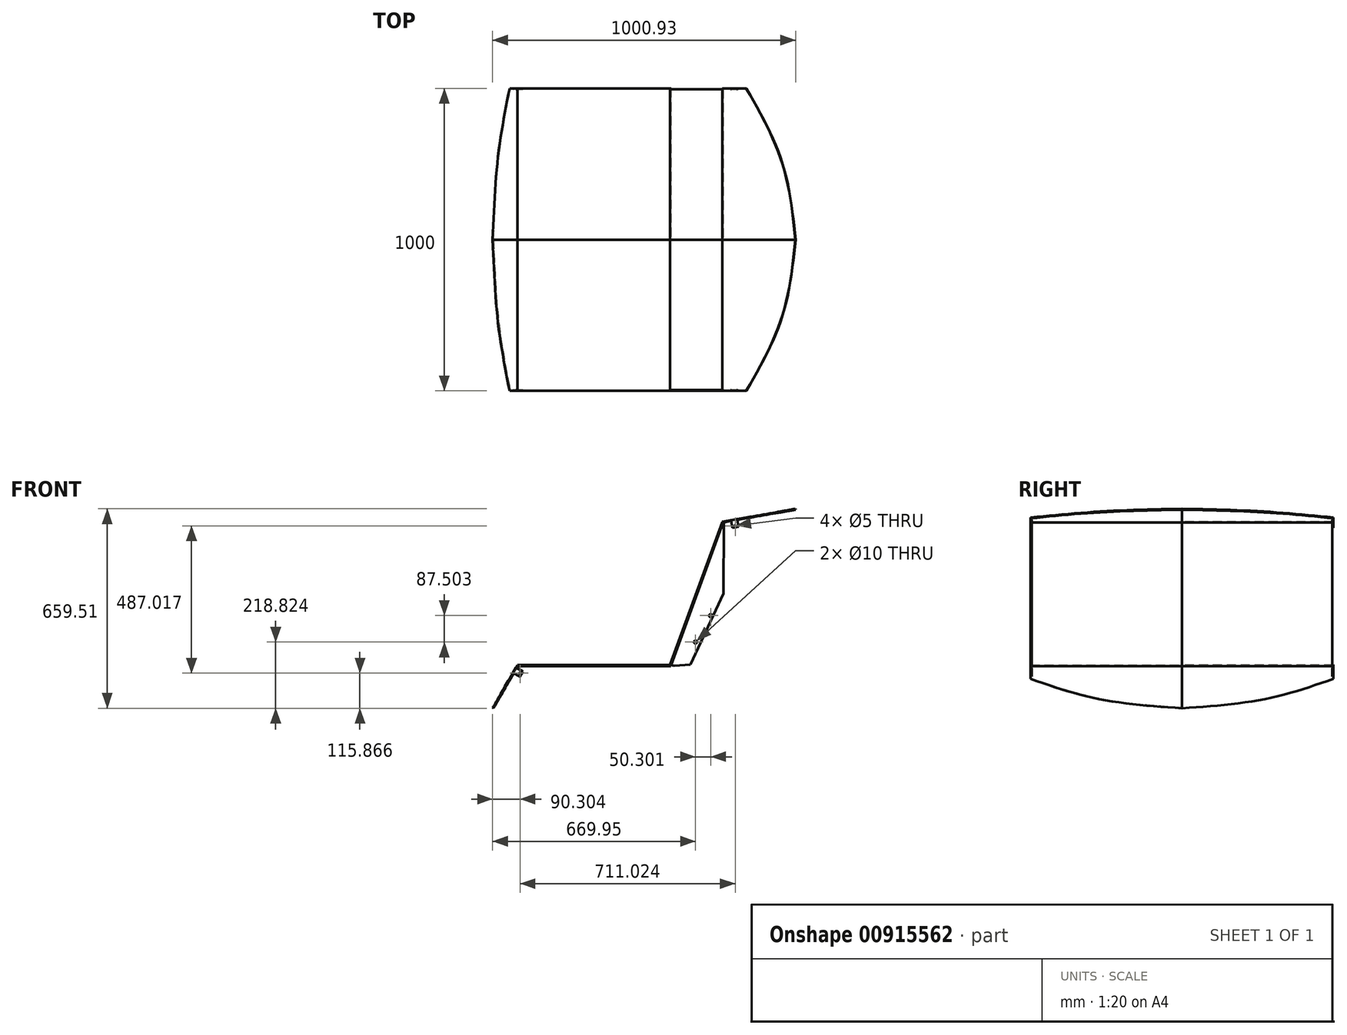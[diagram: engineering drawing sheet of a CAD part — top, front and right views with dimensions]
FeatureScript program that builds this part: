
annotation { "Feature Type Name" : "Feature", "Feature Type Description" : "" }
export const myFeature = defineFeature(function(context is Context, id is Id, definition is map)
    precondition{}
    {
        {
            var Q0;
            Q0=qCreatedBy(makeId("Front.planeOp"),FACE);
            var sketch = newSketch(context, id + "F0", { "sketchPlane" : qUnion([Q0])});
            skLineSegment(sketch, "E0", {"start": v(0, 0) * mm, "end": v(504.47, 0) * mm});
            skLineSegment(sketch, "E1", {"start": v(0, 0) * mm, "end": v(-81.6, -141.33) * mm});
            skLineSegment(sketch, "E2", {"start": v(504.47, 0) * mm, "end": v(677, 474.05) * mm});
            skLineSegment(sketch, "E3", {"start": v(677, 474.05) * mm, "end": v(918.8, 516.68) * mm});
            skLineSegment(sketch, "E4.0", {"start": v(679.24, 471.4) * mm, "end": v(919.33, 513.73) * mm});
            skLineSegment(sketch, "E4.1", {"start": v(506.57, -3) * mm, "end": v(679.24, 471.4) * mm});
            skLineSegment(sketch, "E4.2", {"start": v(1.73, -3) * mm, "end": v(506.57, -3) * mm});
            skLineSegment(sketch, "E4.3", {"start": v(1.73, -3) * mm, "end": v(-79, -142.83) * mm});
            skLineSegment(sketch, "E5", {"start": v(-79, -142.83) * mm, "end": v(-81.6, -141.33) * mm});
            skLineSegment(sketch, "E6", {"start": v(919.33, 513.73) * mm, "end": v(918.8, 516.68) * mm});
            skSolve(sketch);
        }
        {
            var Q0;
            Q0=makeQuery(id+"F0.imprint","IMPRINT",FACE,{"disambiguationData":[TD([[makeQuery(id+"F0.imprint","IMPRINT",EDGE,{"derivedFrom":sQuery(id+"F0.wireOp",EDGE,"E0")}),-1.0]])]});
            extrude(context, id + "F1", {"entities" : qUnion([Q0]), "depth" : 500 * mm, "offsetDistance" : 25 * mm});
        }
        {
            var Q0;
            Q0=makeQuery(id+"F1.opExtrude","SWEPT_FACE",FACE,{"disambiguationData":[OSD([sQuery(id+"F0.wireOp",EDGE,"E1")])]});
            var sketch = newSketch(context, id + "F2", { "sketchPlane" : qUnion([Q0])});
            skLineSegment(sketch, "E7", {"start": v(0, -163.2) * mm, "end": v(0, 586.8) * mm, "construction": true});
            skLineSegment(sketch, "E8", {"start": v(500, 0) * mm, "end": v(500, -51.4) * mm, "construction": true});
            skFitSpline(sketch, "E9", {"points": [v(0, -163.2) * mm, v(271.48, -128.56) * mm, v(500, -51.4) * mm], "startDerivative": vector(540.37, 43.35) * mm, "endDerivative": vector(458.78, 181.7) * mm});
            skLineSegment(sketch, "E10", {"start": v(500, -51.4) * mm, "end": v(528.77, -51.4) * mm});
            skLineSegment(sketch, "E11", {"start": v(528.77, -51.4) * mm, "end": v(528.77, -174.68) * mm});
            skLineSegment(sketch, "E12", {"start": v(528.77, -174.68) * mm, "end": v(0, -174.68) * mm});
            skLineSegment(sketch, "E13", {"start": v(0, -174.68) * mm, "end": v(0, -163.2) * mm});
            skSolve(sketch);
        }
        {
            var Q0;
            Q0 = qSketchRegion(id + "F2", true);
            extrude(context, id + "F3", {"entities" : qUnion([Q0]), "operationType" : NewBodyOperationType.REMOVE, "oppositeDirection" : true, "depth" : 25 * mm, "offsetDistance" : 25 * mm});
        }
        {
            var Q0;
            Q0=makeQuery(id+"F1.opExtrude","SWEPT_FACE",FACE,{"disambiguationData":[OSD([sQuery(id+"F0.wireOp",EDGE,"E3")])]});
            var sketch = newSketch(context, id + "F4", { "sketchPlane" : qUnion([Q0])});
            skLineSegment(sketch, "E14", {"start": v(749.04, -500) * mm, "end": v(829.72, -500) * mm, "construction": true});
            skFitSpline(sketch, "E15", {"points": [v(994.57, 0) * mm, v(948.78, -256.82) * mm, v(829.72, -500) * mm], "startDerivative": vector(-56.9, -527.53) * mm, "endDerivative": vector(-272.14, -472.64) * mm});
            skLineSegment(sketch, "E16", {"start": v(994.57, 0) * mm, "end": v(1016.99, 0) * mm});
            skLineSegment(sketch, "E17", {"start": v(1016.99, 0) * mm, "end": v(1016.99, -521.85) * mm});
            skLineSegment(sketch, "E18", {"start": v(1016.99, -521.85) * mm, "end": v(833.8, -521.85) * mm});
            skLineSegment(sketch, "E19", {"start": v(833.8, -521.85) * mm, "end": v(829.72, -500) * mm});
            skSolve(sketch);
        }
        {
            var Q0;
            {var subQ0=sQuery(id+"F4.wireOp",EDGE,"E15");Q0=makeQuery(id+"F4.imprint","IMPRINT",FACE,{"disambiguationData":[TD([[makeQuery(id+"F4.imprint","IMPRINT",EDGE,{"derivedFrom":subQ0}),1.0]])]});}
            extrude(context, id + "F5", {"entities" : qUnion([Q0]), "operationType" : NewBodyOperationType.REMOVE, "oppositeDirection" : true, "depth" : 25 * mm, "offsetDistance" : 25 * mm});
        }
        {
            var Q0;
            Q0=makeQuery(id+"F1.opExtrude","SWEPT_FACE",FACE,{"disambiguationData":[OSD([sQuery(id+"F0.wireOp",EDGE,"E1")])]});
            var sketch = newSketch(context, id + "F6", { "sketchPlane" : qUnion([Q0])});
            skLineSegment(sketch, "E20", {"start": v(500, -51.4) * mm, "end": v(500, -30) * mm, "construction": true});
            skLineSegment(sketch, "E21", {"start": v(500, -30) * mm, "end": v(497, -30) * mm});
            skLineSegment(sketch, "E22", {"start": v(497, -30) * mm, "end": v(497, -8) * mm});
            skLineSegment(sketch, "E23", {"start": v(497, -8) * mm, "end": v(500, -8) * mm});
            skLineSegment(sketch, "E24", {"start": v(500, -8) * mm, "end": v(500, -30) * mm});
            skSolve(sketch);
        }
        {
            var Q0;
            Q0 = qSketchRegion(id + "F6", true);
            extrude(context, id + "F7", {"entities" : qUnion([Q0]), "operationType" : NewBodyOperationType.REMOVE, "oppositeDirection" : true, "depth" : 25 * mm, "offsetDistance" : 25 * mm});
        }
        {
            var Q0;
            Q0=makeQuery(id+"F1.opExtrude","SWEPT_FACE",FACE,{"disambiguationData":[OSD([sQuery(id+"F0.wireOp",EDGE,"E3")])]});
            var sketch = newSketch(context, id + "F8", { "sketchPlane" : qUnion([Q0])});
            skLineSegment(sketch, "E25", {"start": v(749.04, -500) * mm, "end": v(777.68, -500) * mm, "construction": true});
            skLineSegment(sketch, "E26", {"start": v(777.68, -500) * mm, "end": v(777.68, -497) * mm});
            skLineSegment(sketch, "E27", {"start": v(777.68, -497) * mm, "end": v(799.68, -497) * mm});
            skLineSegment(sketch, "E28", {"start": v(799.68, -497) * mm, "end": v(799.68, -500) * mm});
            skPoint(sketch, "E28.endSnap0", {"position": v(763.36, -500) * mm});
            skLineSegment(sketch, "E29", {"start": v(799.68, -500) * mm, "end": v(777.68, -500) * mm});
            skSolve(sketch);
        }
        {
            var Q0;
            Q0=makeQuery(id+"F8.imprint","IMPRINT",FACE,{"disambiguationData":[TD([[makeQuery(id+"F8.imprint","IMPRINT",EDGE,{"derivedFrom":sQuery(id+"F8.wireOp",EDGE,"E26")}),-1.0]])]});
            extrude(context, id + "F9", {"entities" : qUnion([Q0]), "operationType" : NewBodyOperationType.REMOVE, "oppositeDirection" : true, "depth" : 25 * mm, "offsetDistance" : 25 * mm});
        }
        {
            var Q0;
            Q0=makeQuery(id+"F9.boolean.opBoolean","COPY",FACE,{"derivedFrom":makeQuery(id+"F9.opExtrude","SWEPT_FACE",FACE,{"disambiguationData":[OSD([sQuery(id+"F8.wireOp",EDGE,"E27")])]})});
            var sketch = newSketch(context, id + "F10", { "sketchPlane" : qUnion([Q0])});
            skLineSegment(sketch, "E30", {"start": v(726.88, 482.84) * mm, "end": v(725.9, 482.67) * mm, "construction": true});
            skLineSegment(sketch, "E31", {"start": v(705.21, 479.02) * mm, "end": v(706.2, 479.2) * mm, "construction": true});
            skLineSegment(sketch, "E32", {"start": v(725.9, 482.67) * mm, "end": v(730.44, 456.86) * mm});
            skLineSegment(sketch, "E33", {"start": v(730.44, 456.86) * mm, "end": v(710.75, 453.4) * mm});
            skLineSegment(sketch, "E34", {"start": v(710.75, 453.4) * mm, "end": v(706.2, 479.2) * mm});
            skLineSegment(sketch, "E35", {"start": v(725.9, 482.67) * mm, "end": v(706.2, 479.2) * mm});
            skSolve(sketch);
        }
        {
            var Q0;
            Q0 = qSketchRegion(id + "F10", true);
            extrude(context, id + "F11", {"entities" : qUnion([Q0]), "operationType" : NewBodyOperationType.ADD, "depth" : 3 * mm, "offsetDistance" : 25 * mm});
        }
        {
            var Q0;
            Q0=makeQuery(id+"F11.opExtrude","CAP_EDGE",EDGE,{"disambiguationData":[OSD([sQuery(id+"F10.wireOp",EDGE,"E35")])],"isStart":false});
            var Q1;
            {var subQ0=makeQuery(id+"F1.opExtrude","SWEPT_FACE",FACE,{"disambiguationData":[OSD([sQuery(id+"F0.wireOp",EDGE,"E4.0")])]});Q1=makeQuery(id+"F11.boolean.opBoolean","SPLIT",EDGE,{"disambiguationData":[topologyDisambiguationEdgeConnected([subQ0,makeQuery(id+"F11.opExtrude","CAP_FACE",FACE,{"disambiguationData":[OSD([sQuery(id+"F10.wireOp",EDGE,"E32"),sQuery(id+"F10.wireOp",EDGE,"E33"),sQuery(id+"F10.wireOp",EDGE,"E34"),sQuery(id+"F10.wireOp",EDGE,"E35")])],"isStart":true})])],"derivedFrom":makeQuery(id+"F9.boolean.opBoolean","INTERSECT",EDGE,{"derivedFrom":[subQ0,makeQuery(id+"F9.opExtrude","SWEPT_FACE",FACE,{"disambiguationData":[OSD([sQuery(id+"F8.wireOp",EDGE,"E27")])]})]})});}
            fillet(context, id + "F12", {"entities" : qUnion([Q0, Q1]), "radius" : 1.5 * mm, "tangentPropagation" : true, "allowEdgeOverflow" : false});
        }
        {
            var Q0;
            Q0=makeQuery(id+"F11.opExtrude","CAP_FACE",FACE,{"disambiguationData":[OSD([sQuery(id+"F10.wireOp",EDGE,"E32"),sQuery(id+"F10.wireOp",EDGE,"E33"),sQuery(id+"F10.wireOp",EDGE,"E34"),sQuery(id+"F10.wireOp",EDGE,"E35")])],"isStart":false});
            var sketch = newSketch(context, id + "F13", { "sketchPlane" : qUnion([Q0])});
            skLineSegment(sketch, "E36", {"start": v(709.88, 458.32) * mm, "end": v(729.58, 461.79) * mm, "construction": true});
            skCircle(sketch, "E37", {"center": v(719.73, 460.05) * mm, "radius": 2.5 * mm});
            skSolve(sketch);
        }
        {
            var Q0;
            Q0=makeQuery(id+"F13.imprint","IMPRINT",FACE,{"disambiguationData":[TD([[makeQuery(id+"F13.imprint","IMPRINT",EDGE,{"derivedFrom":sQuery(id+"F13.wireOp",EDGE,"E37")}),1.0]])]});
            extrude(context, id + "F14", {"entities" : qUnion([Q0]), "operationType" : NewBodyOperationType.REMOVE, "oppositeDirection" : true, "depth" : 25 * mm, "offsetDistance" : 25 * mm});
        }
        {
            var Q0;
            Q0=makeQuery(id+"F7.boolean.opBoolean","COPY",FACE,{"derivedFrom":makeQuery(id+"F7.opExtrude","SWEPT_FACE",FACE,{"disambiguationData":[OSD([sQuery(id+"F6.wireOp",EDGE,"E22")])]})});
            var sketch = newSketch(context, id + "F15", { "sketchPlane" : qUnion([Q0])});
            skLineSegment(sketch, "E38", {"start": v(-4, -6.93) * mm, "end": v(-4.5, -7.8) * mm, "construction": true});
            skLineSegment(sketch, "E39", {"start": v(-15, -25.98) * mm, "end": v(-14.5, -25.11) * mm, "construction": true});
            skLineSegment(sketch, "E40", {"start": v(-14.5, -25.11) * mm, "end": v(-4.5, -7.8) * mm});
            skLineSegment(sketch, "E41", {"start": v(-4.5, -7.8) * mm, "end": v(18.03, -20.8) * mm});
            skPoint(sketch, "E42.end.orphan", {"position": v(0, -29.45) * mm});
            skLineSegment(sketch, "E43", {"start": v(18.03, -20.8) * mm, "end": v(8.03, -38.12) * mm});
            skLineSegment(sketch, "E44", {"start": v(8.03, -38.12) * mm, "end": v(-14.5, -25.11) * mm});
            skSolve(sketch);
        }
        {
            var Q0;
            Q0 = qSketchRegion(id + "F15", true);
            extrude(context, id + "F16", {"entities" : qUnion([Q0]), "operationType" : NewBodyOperationType.ADD, "depth" : 3 * mm, "offsetDistance" : 25 * mm});
        }
        {
            var Q0;
            Q0=makeQuery(id+"F16.opExtrude","CAP_EDGE",EDGE,{"disambiguationData":[OSD([sQuery(id+"F15.wireOp",EDGE,"E40")])],"isStart":false});
            var Q1;
            {var subQ0=makeQuery(id+"F1.opExtrude","SWEPT_FACE",FACE,{"disambiguationData":[OSD([sQuery(id+"F0.wireOp",EDGE,"E4.3")])]});Q1=makeQuery(id+"F16.boolean.opBoolean","SPLIT",EDGE,{"disambiguationData":[topologyDisambiguationEdgeConnected([subQ0,makeQuery(id+"F16.opExtrude","CAP_FACE",FACE,{"disambiguationData":[OSD([sQuery(id+"F15.wireOp",EDGE,"E40"),sQuery(id+"F15.wireOp",EDGE,"E41"),sQuery(id+"F15.wireOp",EDGE,"E43"),sQuery(id+"F15.wireOp",EDGE,"E44")])],"isStart":true})])],"derivedFrom":makeQuery(id+"F7.boolean.opBoolean","INTERSECT",EDGE,{"derivedFrom":[subQ0,makeQuery(id+"F7.opExtrude","SWEPT_FACE",FACE,{"disambiguationData":[OSD([sQuery(id+"F6.wireOp",EDGE,"E22")])]})]})});}
            fillet(context, id + "F17", {"entities" : qUnion([Q0, Q1]), "radius" : 1.5 * mm, "tangentPropagation" : true, "allowEdgeOverflow" : false});
        }
        {
            var Q0;
            Q0=makeQuery(id+"F16.opExtrude","CAP_FACE",FACE,{"disambiguationData":[OSD([sQuery(id+"F15.wireOp",EDGE,"E40"),sQuery(id+"F15.wireOp",EDGE,"E41"),sQuery(id+"F15.wireOp",EDGE,"E43"),sQuery(id+"F15.wireOp",EDGE,"E44")])],"isStart":false});
            var sketch = newSketch(context, id + "F18", { "sketchPlane" : qUnion([Q0])});
            skLineSegment(sketch, "E45", {"start": v(13.7, -18.3) * mm, "end": v(3.7, -35.62) * mm, "construction": true});
            skCircle(sketch, "E46", {"center": v(8.7, -26.96) * mm, "radius": 2.5 * mm});
            skSolve(sketch);
        }
        {
            var Q0;
            Q0 = qSketchRegion(id + "F18", true);
            extrude(context, id + "F19", {"entities" : qUnion([Q0]), "operationType" : NewBodyOperationType.REMOVE, "oppositeDirection" : true, "depth" : 25 * mm, "offsetDistance" : 25 * mm});
        }
        {
            var Q0;
            Q0=makeQuery(id+"F1.opExtrude","SWEPT_FACE",FACE,{"disambiguationData":[OSD([sQuery(id+"F0.wireOp",EDGE,"E2")])]});
            var sketch = newSketch(context, id + "F20", { "sketchPlane" : qUnion([Q0])});
            skLineSegment(sketch, "E47", {"start": v(500, 677) * mm, "end": v(500, 676) * mm, "construction": true});
            skLineSegment(sketch, "E48", {"start": v(500, 676) * mm, "end": v(497, 676) * mm});
            skLineSegment(sketch, "E49", {"start": v(497, 676) * mm, "end": v(497, 173.54) * mm});
            skLineSegment(sketch, "E50", {"start": v(497, 173.54) * mm, "end": v(500, 173.54) * mm});
            skSolve(sketch);
        }
        {
            var Q0;
            Q0 = qSketchRegion(id + "F20", true);
            var Q1;
            {var subQ0=sQuery(id+"F20.wireOp",EDGE,"E48");Q1=makeQuery(id+"F20.imprint","IMPRINT",FACE,{"disambiguationData":[TD([[makeQuery(id+"F20.imprint","IMPRINT",EDGE,{"derivedFrom":subQ0}),1.0]])]});}
            extrude(context, id + "F21", {"entities" : qUnion([Q0, Q1]), "operationType" : NewBodyOperationType.REMOVE, "oppositeDirection" : true, "depth" : 25 * mm, "offsetDistance" : 25 * mm});
        }
        {
            var Q0;
            Q0=makeQuery(id+"F21.boolean.opBoolean","COPY",FACE,{"derivedFrom":makeQuery(id+"F21.opExtrude","SWEPT_FACE",FACE,{"disambiguationData":[OSD([sQuery(id+"F20.wireOp",EDGE,"E49")])]})});
            var sketch = newSketch(context, id + "F22", { "sketchPlane" : qUnion([Q0])});
            skLineSegment(sketch, "E51", {"start": v(676.67, 473.1) * mm, "end": v(676.32, 472.17) * mm, "construction": true});
            skLineSegment(sketch, "E52", {"start": v(676.32, 472.17) * mm, "end": v(681.96, 470.12) * mm});
            skLineSegment(sketch, "E53", {"start": v(601.23, 265.83) * mm, "end": v(680.73, 236.9) * mm, "construction": true});
            skLineSegment(sketch, "E54", {"start": v(676.32, 472.17) * mm, "end": v(755.83, 443.23) * mm, "construction": true});
            skLineSegment(sketch, "E55", {"start": v(679.54, 233.63) * mm, "end": v(755.83, 443.23) * mm, "construction": true});
            skPoint(sketch, "E56.end.orphan", {"position": v(680.68, 337.59) * mm});
            skLineSegment(sketch, "E57", {"start": v(681.96, 470.12) * mm, "end": v(680.73, 236.9) * mm});
            skLineSegment(sketch, "E58", {"start": v(680.73, 236.9) * mm, "end": v(592.08, -6.66) * mm, "construction": true});
            skLineSegment(sketch, "E59", {"start": v(592.08, -6.66) * mm, "end": v(571.2, 0.94) * mm, "construction": true});
            skLineSegment(sketch, "E60", {"start": v(680.73, 236.9) * mm, "end": v(571.2, 0.94) * mm});
            skLineSegment(sketch, "E61", {"start": v(504.81, 0.94) * mm, "end": v(505.15, 1.88) * mm, "construction": true});
            skLineSegment(sketch, "E62", {"start": v(505.15, 1.88) * mm, "end": v(518.28, -2.9) * mm});
            skLineSegment(sketch, "E63", {"start": v(518.28, -2.9) * mm, "end": v(571.2, 0.94) * mm});
            skSolve(sketch);
        }
        {
            var Q0;
            {var subQ0=sQuery(id+"F22.wireOp",EDGE,"E52");var subQ1=sQuery(id+"F20.wireOp",EDGE,"E49");var subQ2=makeQuery(id+"F21.boolean.opBoolean","COPY",EDGE,{"derivedFrom":makeQuery(id+"F21.opExtrude","CAP_EDGE",EDGE,{"disambiguationData":[OSD([subQ1])],"isStart":true})});var subQ3=makeQuery(id+"F22.imprint","INTERSECT",VERTEX,{"derivedFrom":[subQ2,subQ0]});Q0=makeQuery(id+"F22.imprint","IMPRINT",FACE,{"disambiguationData":[TD([[makeQuery(id+"F22.imprint","IMPRINT",EDGE,{"disambiguationData":[TD([[subQ3,-1.0]])],"derivedFrom":subQ2}),1.0]])]});}
            var Q1;
            {var subQ4=sQuery(id+"F22.wireOp",EDGE,"E57");Q1=makeQuery(id+"F22.imprint","IMPRINT",FACE,{"disambiguationData":[TD([[makeQuery(id+"F22.imprint","IMPRINT",EDGE,{"derivedFrom":subQ4}),-1.0]])]});}
            extrude(context, id + "F23", {"entities" : qUnion([Q0, Q1]), "operationType" : NewBodyOperationType.ADD, "depth" : 3 * mm, "offsetDistance" : 25 * mm});
        }
        {
            var Q0;
            Q0=makeQuery(id+"F23.opExtrude","CAP_FACE",FACE,{"disambiguationData":[OSD([sQuery(id+"F20.wireOp",EDGE,"E49"),sQuery(id+"F22.wireOp",EDGE,"E52"),sQuery(id+"F22.wireOp",EDGE,"E57"),sQuery(id+"F22.wireOp",EDGE,"E60"),sQuery(id+"F22.wireOp",EDGE,"E62"),sQuery(id+"F22.wireOp",EDGE,"E63")])],"isStart":false});
            var sketch = newSketch(context, id + "F24", { "sketchPlane" : qUnion([Q0])});
            skLineSegment(sketch, "E64", {"start": v(511.72, -0.5) * mm, "end": v(545.27, 91.67) * mm, "construction": true});
            skLineSegment(sketch, "E65", {"start": v(538.7, 94.06) * mm, "end": v(588.35, 76) * mm, "construction": true});
            skCircle(sketch, "E66", {"center": v(588.35, 76) * mm, "radius": 5 * mm});
            skLineSegment(sketch, "E67", {"start": v(514.1, -1.38) * mm, "end": v(581.67, 184.24) * mm, "construction": true});
            skLineSegment(sketch, "E68", {"start": v(572.71, 187.5) * mm, "end": v(638.65, 163.5) * mm, "construction": true});
            skCircle(sketch, "E69", {"center": v(638.65, 163.5) * mm, "radius": 5 * mm});
            skSolve(sketch);
        }
        {
            var Q0;
            Q0 = qSketchRegion(id + "F24", true);
            extrude(context, id + "F25", {"entities" : qUnion([Q0]), "operationType" : NewBodyOperationType.REMOVE, "oppositeDirection" : true, "depth" : 25 * mm, "offsetDistance" : 25 * mm});
        }
        {
            var Q0;
            Q0=makeQuery(id+"F1.opExtrude","SWEPT_BODY",BODY,{"disambiguationData":[OSD([sQuery(id+"F0.wireOp",EDGE,"E0"),sQuery(id+"F0.wireOp",EDGE,"E1"),sQuery(id+"F0.wireOp",EDGE,"E2"),sQuery(id+"F0.wireOp",EDGE,"E3"),sQuery(id+"F0.wireOp",EDGE,"E4.0"),sQuery(id+"F0.wireOp",EDGE,"E4.1"),sQuery(id+"F0.wireOp",EDGE,"E4.2"),sQuery(id+"F0.wireOp",EDGE,"E4.3"),sQuery(id+"F0.wireOp",EDGE,"E5"),sQuery(id+"F0.wireOp",EDGE,"E6")])]});
            var Q1;
            Q1=makeQuery(id+"F1.opExtrude","CAP_FACE",FACE,{"disambiguationData":[OSD([sQuery(id+"F0.wireOp",EDGE,"E0"),sQuery(id+"F0.wireOp",EDGE,"E1"),sQuery(id+"F0.wireOp",EDGE,"E2"),sQuery(id+"F0.wireOp",EDGE,"E3"),sQuery(id+"F0.wireOp",EDGE,"E4.0"),sQuery(id+"F0.wireOp",EDGE,"E4.1"),sQuery(id+"F0.wireOp",EDGE,"E4.2"),sQuery(id+"F0.wireOp",EDGE,"E4.3"),sQuery(id+"F0.wireOp",EDGE,"E5"),sQuery(id+"F0.wireOp",EDGE,"E6")])],"isStart":true});
            mirror(context, id + "F26", {"operationType" : NewBodyOperationType.ADD, "entities" : qUnion([Q0]), "mirrorPlane" : qUnion([Q1])});
        }
    });
